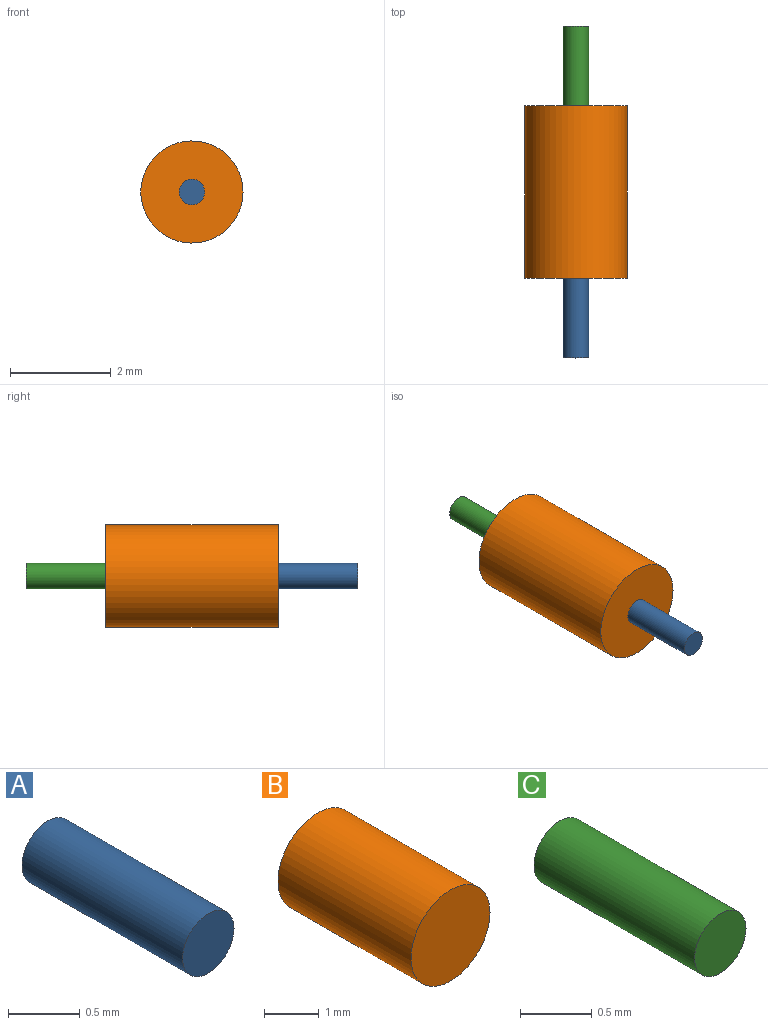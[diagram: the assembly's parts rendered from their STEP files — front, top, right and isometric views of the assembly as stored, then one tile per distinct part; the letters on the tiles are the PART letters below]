
ASSEMBLY  parts=3 mates=2
PART A: 3 faces, bbox 0.5x1.6x0.5 mm
  f0: cylinder r=0.25mm len=1.59mm, axis (0,1,0), area 2.5mm2, adj f1,f2
  f1: plane 0.51x0.51mm, normal (0,-1,0), area 0.2mm2, adj f0
  f2: plane 0.51x0.51mm, normal (0,1,0), area 0.2mm2, adj f0
PART B: 3 faces, bbox 2x3.4x2 mm
  f0: cylinder r=1.02mm len=3.43mm, axis (0,-1,0), area 21.9mm2, adj f1,f2
  f1: plane 2.03x2.03mm, normal (0,1,0), area 3.2mm2, adj f0
  f2: plane 2.03x2.03mm, normal (0,-1,0), area 3.2mm2, adj f0
PART C: 3 faces, bbox 0.5x1.6x0.5 mm
  f0: cylinder r=0.25mm len=1.59mm, axis (0,1,0), area 2.5mm2, adj f1,f2
  f1: plane 0.51x0.51mm, normal (0,-1,0), area 0.2mm2, adj f0
  f2: plane 0.51x0.51mm, normal (0,1,0), area 0.2mm2, adj f0
PLACE A t=(-3.04,-0.57,0.12)mm
PLACE B t=(-0.83,-0.57,0.86)mm
PLACE C t=(-5.58,4.44,0.12)mm
MATE fastened A.f0 <-> B.f0  axis (0,1,0) through (-0.83,-0.57,0.86)mm
MATE fastened C.f0 <-> B.f0  axis (0,1,0) through (-0.83,2.86,0.86)mm
